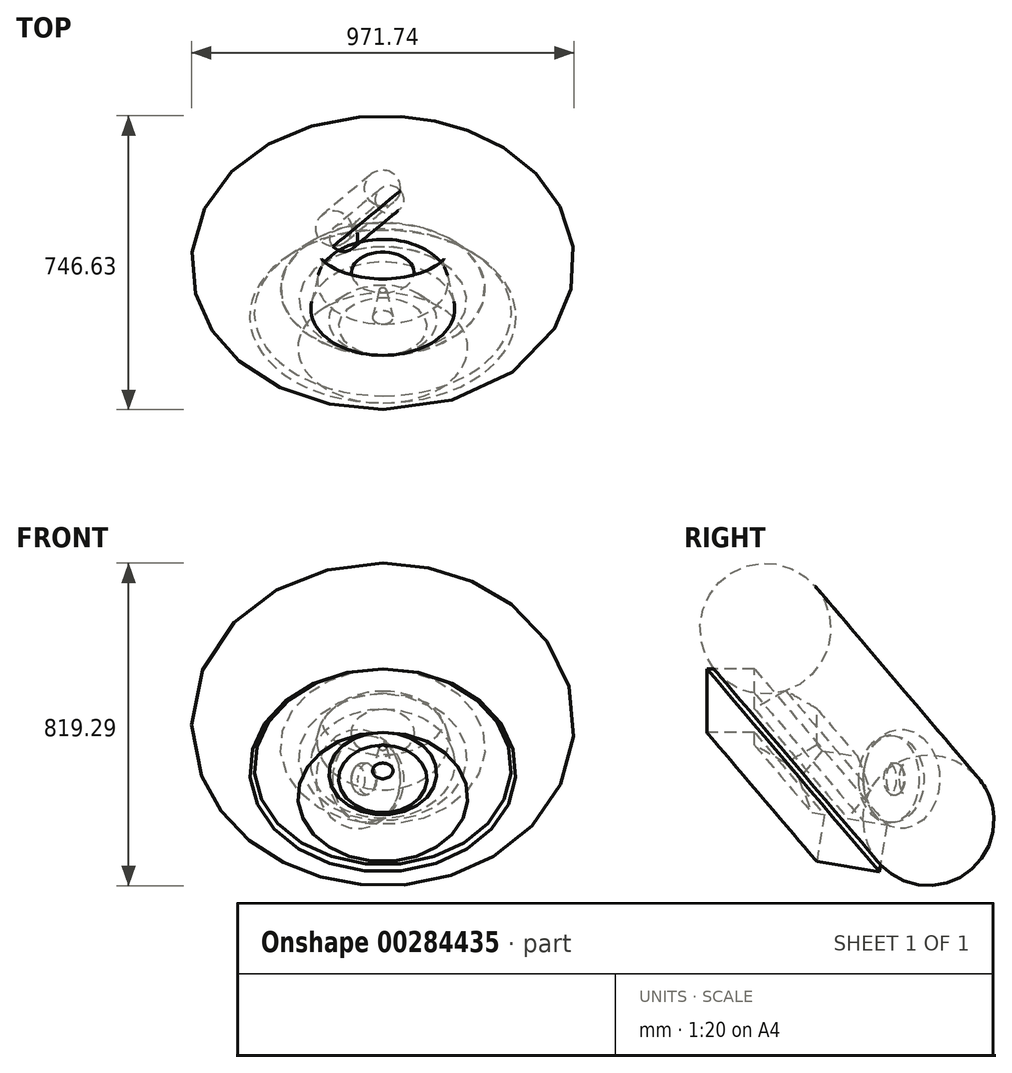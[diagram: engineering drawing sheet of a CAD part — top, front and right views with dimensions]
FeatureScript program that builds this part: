
annotation { "Feature Type Name" : "Feature", "Feature Type Description" : "" }
export const myFeature = defineFeature(function(context is Context, id is Id, definition is map)
    precondition{}
    {
        {
            var Q0;
            Q0=qCreatedBy(makeId("Top.planeOp"),FACE);
            var sketch = newSketch(context, id + "F0", { "sketchPlane" : qUnion([Q0])});
            skCircle(sketch, "E0", {"center": v(-124.74, -15.5) * mm, "radius": 45.48 * mm});
            skCircle(sketch, "E1", {"center": v(-99, -38.32) * mm, "radius": 35.45 * mm});
            skLineSegment(sketch, "E2", {"start": v(-99.15, 80.04) * mm, "end": v(40.49, -88.78) * mm});
            skSolve(sketch);
        }
        {
            var Q0;
            {var subQ0=sQuery(id+"F0.wireOp",EDGE,"E1");var subQ1=sQuery(id+"F0.wireOp",EDGE,"E0");var subQ2=makeQuery(id+"F0.imprint","INTERSECT",VERTEX,{"disambiguationData":[OD(0.0)],"derivedFrom":[subQ1,subQ0]});Q0=makeQuery(id+"F0.imprint","IMPRINT",FACE,{"disambiguationData":[TD([[makeQuery(id+"F0.imprint","IMPRINT",EDGE,{"disambiguationData":[TD([[subQ2,1.0]])],"derivedFrom":subQ1}),1.0]])]});}
            var Q1;
            {var subQ0=sQuery(id+"F0.wireOp",EDGE,"E1");var subQ1=sQuery(id+"F0.wireOp",EDGE,"E0");var subQ2=makeQuery(id+"F0.imprint","INTERSECT",VERTEX,{"disambiguationData":[OD(0.0)],"derivedFrom":[subQ1,subQ0]});Q1=makeQuery(id+"F0.imprint","IMPRINT",FACE,{"disambiguationData":[TD([[makeQuery(id+"F0.imprint","IMPRINT",EDGE,{"disambiguationData":[TD([[subQ2,-1.0]])],"derivedFrom":subQ1}),-1.0]])]});}
            var Q2;
            Q2=sQuery(id+"F0.wireOp",EDGE,"E2");
            revolve(context, id + "F1", {"entities" : qUnion([Q0, Q1]), "axis" : qUnion([Q2]), "revolveType" : RevolveType.FULL});
        }
        {
            var Q0;
            Q0=qCreatedBy(makeId("Right.planeOp"),FACE);
            var sketch = newSketch(context, id + "F2", { "sketchPlane" : qUnion([Q0])});
            skCircle(sketch, "E3.cCircle", {"center": v(-258.24, 132.43) * mm, "radius": 79.63 * mm, "construction": true});
            skLineSegment(sketch, "E3.0", {"start": v(-178.6, 178.4) * mm, "end": v(-178.6, 86.45) * mm});
            skLineSegment(sketch, "E3.1", {"start": v(-178.6, 86.45) * mm, "end": v(-258.24, 40.48) * mm});
            skLineSegment(sketch, "E3.2", {"start": v(-258.24, 40.48) * mm, "end": v(-337.88, 86.45) * mm});
            skLineSegment(sketch, "E3.3", {"start": v(-337.88, 86.45) * mm, "end": v(-337.88, 178.4) * mm});
            skLineSegment(sketch, "E3.4", {"start": v(-337.88, 178.4) * mm, "end": v(-258.24, 224.39) * mm});
            skLineSegment(sketch, "E3.5", {"start": v(-258.24, 224.39) * mm, "end": v(-178.6, 178.4) * mm});
            skPoint(sketch, "E3.0.midPoint", {"position": v(-178.6, 132.43) * mm});
            skCircle(sketch, "E4", {"center": v(-309.78, 382.3) * mm, "radius": 166.1 * mm});
            skLineSegment(sketch, "E5.bottom", {"start": v(-458.61, 279.94) * mm, "end": v(-337.88, 279.94) * mm});
            skLineSegment(sketch, "E5.top", {"start": v(-458.61, 118.9) * mm, "end": v(-337.88, 118.9) * mm});
            skLineSegment(sketch, "E5.left", {"start": v(-458.61, 279.94) * mm, "end": v(-458.61, 118.9) * mm});
            skLineSegment(sketch, "E5.right", {"start": v(-337.88, 279.94) * mm, "end": v(-337.88, 118.9) * mm});
            skLineSegment(sketch, "E6", {"start": v(39.48, 259.6) * mm, "end": v(-350.88, -72.53) * mm});
            skSolve(sketch);
        }
        {
            var Q0;
            {var subQ2=sQuery(id+"F2.wireOp",EDGE,"E5.right");var subQ4=sQuery(id+"F2.wireOp",EDGE,"E5.bottom");var subQ6=makeQuery(id+"F2.imprint","INTERSECT",VERTEX,{"derivedFrom":[subQ4,subQ2]});Q0=makeQuery(id+"F2.imprint","IMPRINT",FACE,{"disambiguationData":[TD([[makeQuery(id+"F2.imprint","IMPRINT",EDGE,{"disambiguationData":[TD([[subQ6,1.0]])],"derivedFrom":subQ4}),1.0]])]});}
            var Q1;
            {var subQ1=sQuery(id+"F2.wireOp",EDGE,"E4");var subQ6=sQuery(id+"F2.wireOp",EDGE,"E5.bottom");var subQ9=makeQuery(id+"F2.imprint","INTERSECT",VERTEX,{"derivedFrom":[subQ1,subQ6]});Q1=makeQuery(id+"F2.imprint","IMPRINT",FACE,{"disambiguationData":[TD([[makeQuery(id+"F2.imprint","IMPRINT",EDGE,{"disambiguationData":[TD([[subQ9,-1.0]])],"derivedFrom":subQ1}),-1.0]])]});}
            var Q2;
            {var subQ1=sQuery(id+"F2.wireOp",EDGE,"E5.top");Q2=makeQuery(id+"F2.imprint","IMPRINT",FACE,{"disambiguationData":[TD([[makeQuery(id+"F2.imprint","IMPRINT",EDGE,{"derivedFrom":subQ1}),1.0]])]});}
            var Q3;
            {var subQ1=sQuery(id+"F2.wireOp",EDGE,"E3.0");Q3=makeQuery(id+"F2.imprint","IMPRINT",FACE,{"disambiguationData":[TD([[makeQuery(id+"F2.imprint","IMPRINT",EDGE,{"derivedFrom":subQ1}),-1.0]])]});}
            var Q4;
            {var subQ0=sQuery(id+"F2.wireOp",EDGE,"E3.5");var subQ3=sQuery(id+"F2.wireOp",EDGE,"E6");var subQ5=makeQuery(id+"F2.imprint","INTERSECT",VERTEX,{"derivedFrom":[subQ0,subQ3]});Q4=makeQuery(id+"F2.imprint","IMPRINT",FACE,{"disambiguationData":[TD([[makeQuery(id+"F2.imprint","IMPRINT",EDGE,{"disambiguationData":[TD([[subQ5,-1.0]])],"derivedFrom":subQ3}),-1.0]])]});}
            var Q5;
            Q5=sQuery(id+"F2.wireOp",EDGE,"E6");
            revolve(context, id + "F3", {"entities" : qUnion([Q0, Q1, Q2, Q3, Q4]), "axis" : qUnion([Q5]), "revolveType" : RevolveType.FULL});
        }
    });
